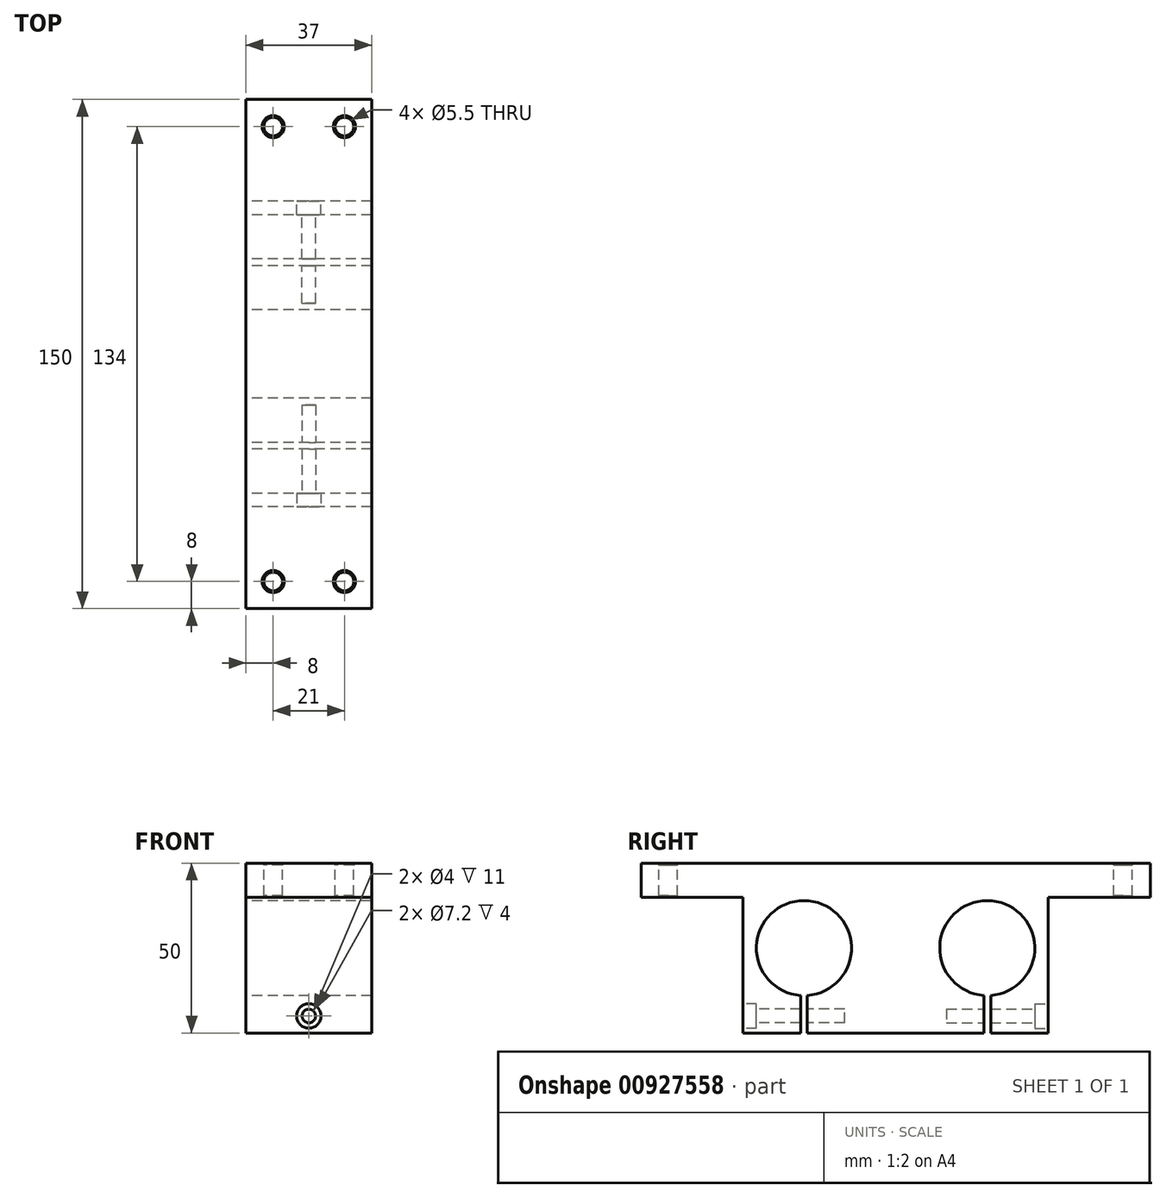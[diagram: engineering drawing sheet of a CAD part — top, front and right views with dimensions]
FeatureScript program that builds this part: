
annotation { "Feature Type Name" : "Feature", "Feature Type Description" : "" }
export const myFeature = defineFeature(function(context is Context, id is Id, definition is map)
    precondition{}
    {
        {
            var Q0;
            Q0=qCreatedBy(makeId("Right.planeOp"),FACE);
            var sketch = newSketch(context, id + "F0", { "sketchPlane" : qUnion([Q0])});
            skLineSegment(sketch, "E0.bottom", {"start": v(-45, -40) * mm, "end": v(-28, -40) * mm});
            skLineSegment(sketch, "E0.left", {"start": v(-45, -40) * mm, "end": v(-45, 0) * mm});
            skLineSegment(sketch, "E0.right", {"start": v(45, -40) * mm, "end": v(45, 0) * mm});
            skPoint(sketch, "E0.middle", {"position": v(0, 0) * mm});
            skLineSegment(sketch, "E1", {"start": v(27, 53.53) * mm, "end": v(27, -48.08) * mm, "construction": true});
            skLineSegment(sketch, "E2.MirrorCS", {"start": v(-27, 53.53) * mm, "end": v(-27, -48.08) * mm, "construction": true});
            skArc(sketch, "E3", {"start": v(28, -28.96) * mm, "mid": v(27, -1) * mm, "end": v(26, -28.96) * mm});
            skArc(sketch, "E4.MirrorC", {"start": v(-28, -28.96) * mm, "mid": v(-27, -1) * mm, "end": v(-26, -28.96) * mm});
            skLineSegment(sketch, "E5", {"start": v(28, -28.96) * mm, "end": v(28, -40) * mm});
            skLineSegment(sketch, "E6.MirrorCS", {"start": v(26, -28.96) * mm, "end": v(26, -40) * mm});
            skLineSegment(sketch, "E7.MirrorCS", {"start": v(-26, -28.96) * mm, "end": v(-26, -40) * mm});
            skLineSegment(sketch, "E8.MirrorCS", {"start": v(-28, -28.96) * mm, "end": v(-28, -40) * mm});
            skLineSegment(sketch, "E9.trimOffspring", {"start": v(28, -40) * mm, "end": v(45, -40) * mm});
            skLineSegment(sketch, "E10.trimOffspring", {"start": v(-26, -40) * mm, "end": v(26, -40) * mm});
            skLineSegment(sketch, "E11", {"start": v(-45, 0) * mm, "end": v(-75, 0) * mm});
            skLineSegment(sketch, "E12", {"start": v(-75, 0) * mm, "end": v(-75, 10) * mm});
            skLineSegment(sketch, "E13", {"start": v(-75, 10) * mm, "end": v(75, 10) * mm});
            skLineSegment(sketch, "E14", {"start": v(75, 10) * mm, "end": v(75, 0) * mm});
            skLineSegment(sketch, "E15", {"start": v(75, 0) * mm, "end": v(45, 0) * mm});
            skSolve(sketch);
        }
        {
            var Q0;
            Q0=makeQuery(id+"F0.imprint","IMPRINT",FACE,{"disambiguationData":[TD([[makeQuery(id+"F0.imprint","IMPRINT",EDGE,{"derivedFrom":sQuery(id+"F0.wireOp",EDGE,"E0.bottom")}),1.0]])]});
            extrude(context, id + "F1", {"entities" : qUnion([Q0]), "depth" : 37 * mm, "offsetDistance" : 25 * mm});
        }
        {
            var Q0;
            Q0=makeQuery(id+"F1.opExtrude","SWEPT_FACE",FACE,{"disambiguationData":[OSD([sQuery(id+"F0.wireOp",EDGE,"E0.left")])]});
            var sketch = newSketch(context, id + "F2", { "sketchPlane" : qUnion([Q0])});
            skLineSegment(sketch, "E16", {"start": v(-5.26, -35) * mm, "end": v(49.02, -35) * mm, "construction": true});
            skCircle(sketch, "E17", {"center": v(18.5, -35) * mm, "radius": 2 * mm});
            skPoint(sketch, "E17.centerSnap0", {"position": v(18.5, -40) * mm});
            skSolve(sketch);
        }
        {
            var Q0;
            Q0 = qSketchRegion(id + "F2", true);
            extrude(context, id + "F3", {"entities" : qUnion([Q0]), "operationType" : NewBodyOperationType.REMOVE, "oppositeDirection" : true, "depth" : 30 * mm, "offsetDistance" : 25 * mm});
        }
        {
            var Q0;
            Q0=makeQuery(id+"F1.opExtrude","SWEPT_FACE",FACE,{"disambiguationData":[OSD([sQuery(id+"F0.wireOp",EDGE,"E0.left")])]});
            var sketch = newSketch(context, id + "F4", { "sketchPlane" : qUnion([Q0])});
            skCircle(sketch, "E18", {"center": v(18.5, -35) * mm, "radius": 3.6 * mm});
            skSolve(sketch);
        }
        {
            var Q0;
            Q0 = qSketchRegion(id + "F4", true);
            extrude(context, id + "F5", {"entities" : qUnion([Q0]), "operationType" : NewBodyOperationType.REMOVE, "oppositeDirection" : true, "depth" : 4 * mm, "offsetDistance" : 25 * mm});
        }
        {
            var Q0;
            Q0=makeQuery(id+"F1.opExtrude","SWEPT_FACE",FACE,{"disambiguationData":[OSD([sQuery(id+"F0.wireOp",EDGE,"E0.right")])]});
            var sketch = newSketch(context, id + "F6", { "sketchPlane" : qUnion([Q0])});
            skLineSegment(sketch, "E19", {"start": v(-45.65, -35) * mm, "end": v(19.3, -35) * mm, "construction": true});
            skCircle(sketch, "E20", {"center": v(-18.5, -35) * mm, "radius": 2 * mm});
            skPoint(sketch, "E20.centerSnap0", {"position": v(-18.5, -40) * mm});
            skSolve(sketch);
        }
        {
            var Q0;
            Q0=makeQuery(id+"F6.imprint","IMPRINT",FACE,{"disambiguationData":[TD([[makeQuery(id+"F6.imprint","IMPRINT",EDGE,{"derivedFrom":sQuery(id+"F6.wireOp",EDGE,"E20")}),1.0]])]});
            extrude(context, id + "F7", {"entities" : qUnion([Q0]), "operationType" : NewBodyOperationType.REMOVE, "oppositeDirection" : true, "depth" : 30 * mm, "offsetDistance" : 25 * mm});
        }
        {
            var Q0;
            Q0=makeQuery(id+"F1.opExtrude","SWEPT_FACE",FACE,{"disambiguationData":[OSD([sQuery(id+"F0.wireOp",EDGE,"E0.right")])]});
            var sketch = newSketch(context, id + "F8", { "sketchPlane" : qUnion([Q0])});
            skCircle(sketch, "E21", {"center": v(-18.5, -35) * mm, "radius": 3.6 * mm});
            skSolve(sketch);
        }
        {
            var Q0;
            Q0 = qSketchRegion(id + "F8", true);
            extrude(context, id + "F9", {"entities" : qUnion([Q0]), "operationType" : NewBodyOperationType.REMOVE, "oppositeDirection" : true, "depth" : 4 * mm, "offsetDistance" : 25 * mm});
        }
        {
            var Q0;
            Q0=makeQuery(id+"F1.opExtrude","SWEPT_FACE",FACE,{"disambiguationData":[OSD([sQuery(id+"F0.wireOp",EDGE,"E13")])]});
            var sketch = newSketch(context, id + "F10", { "sketchPlane" : qUnion([Q0])});
            skLineSegment(sketch, "E22", {"start": v(-23.27, 67) * mm, "end": v(85.09, 67) * mm, "construction": true});
            skCircle(sketch, "E23", {"center": v(29, 67) * mm, "radius": 2.75 * mm});
            skCircle(sketch, "E24", {"center": v(8, 67) * mm, "radius": 2.75 * mm});
            skCircle(sketch, "E25.MirrorC", {"center": v(8, -67) * mm, "radius": 2.75 * mm});
            skCircle(sketch, "E26.MirrorC", {"center": v(29, -67) * mm, "radius": 2.75 * mm});
            skLineSegment(sketch, "E27", {"start": v(18.5, 83.56) * mm, "end": v(18.5, 7.73) * mm, "construction": true});
            skPoint(sketch, "E27.startSnap0", {"position": v(18.5, 75) * mm});
            skSolve(sketch);
        }
        {
            var Q0;
            Q0 = qSketchRegion(id + "F10", true);
            extrude(context, id + "F11", {"entities" : qUnion([Q0]), "operationType" : NewBodyOperationType.REMOVE, "endBound" : BoundingType.THROUGH_ALL, "oppositeDirection" : true, "depth" : 25 * mm, "offsetDistance" : 25 * mm});
        }
        {
            var Q0;
            Q0=makeQuery(id+"F11.boolean.opBoolean","COPY",FACE,{"derivedFrom":makeQuery(id+"F11.opExtrude","SWEPT_FACE",FACE,{"disambiguationData":[OSD([sQuery(id+"F10.wireOp",EDGE,"E24")])]})});
            var Q1;
            Q1=makeQuery(id+"F11.boolean.opBoolean","COPY",FACE,{"derivedFrom":makeQuery(id+"F11.opExtrude","SWEPT_FACE",FACE,{"disambiguationData":[OSD([sQuery(id+"F10.wireOp",EDGE,"E23")])]})});
            var Q2;
            Q2=makeQuery(id+"F11.boolean.opBoolean","COPY",FACE,{"derivedFrom":makeQuery(id+"F11.opExtrude","SWEPT_FACE",FACE,{"disambiguationData":[OSD([sQuery(id+"F10.wireOp",EDGE,"E25.MirrorC")])]})});
            var Q3;
            Q3=makeQuery(id+"F11.boolean.opBoolean","COPY",FACE,{"derivedFrom":makeQuery(id+"F11.opExtrude","SWEPT_FACE",FACE,{"disambiguationData":[OSD([sQuery(id+"F10.wireOp",EDGE,"E26.MirrorC")])]})});
            chamfer(context, id + "F12", {"entities" : qUnion([Q0, Q1, Q2, Q3]), "width" : 0.5 * mm, "tangentPropagation" : true});
        }
    });
